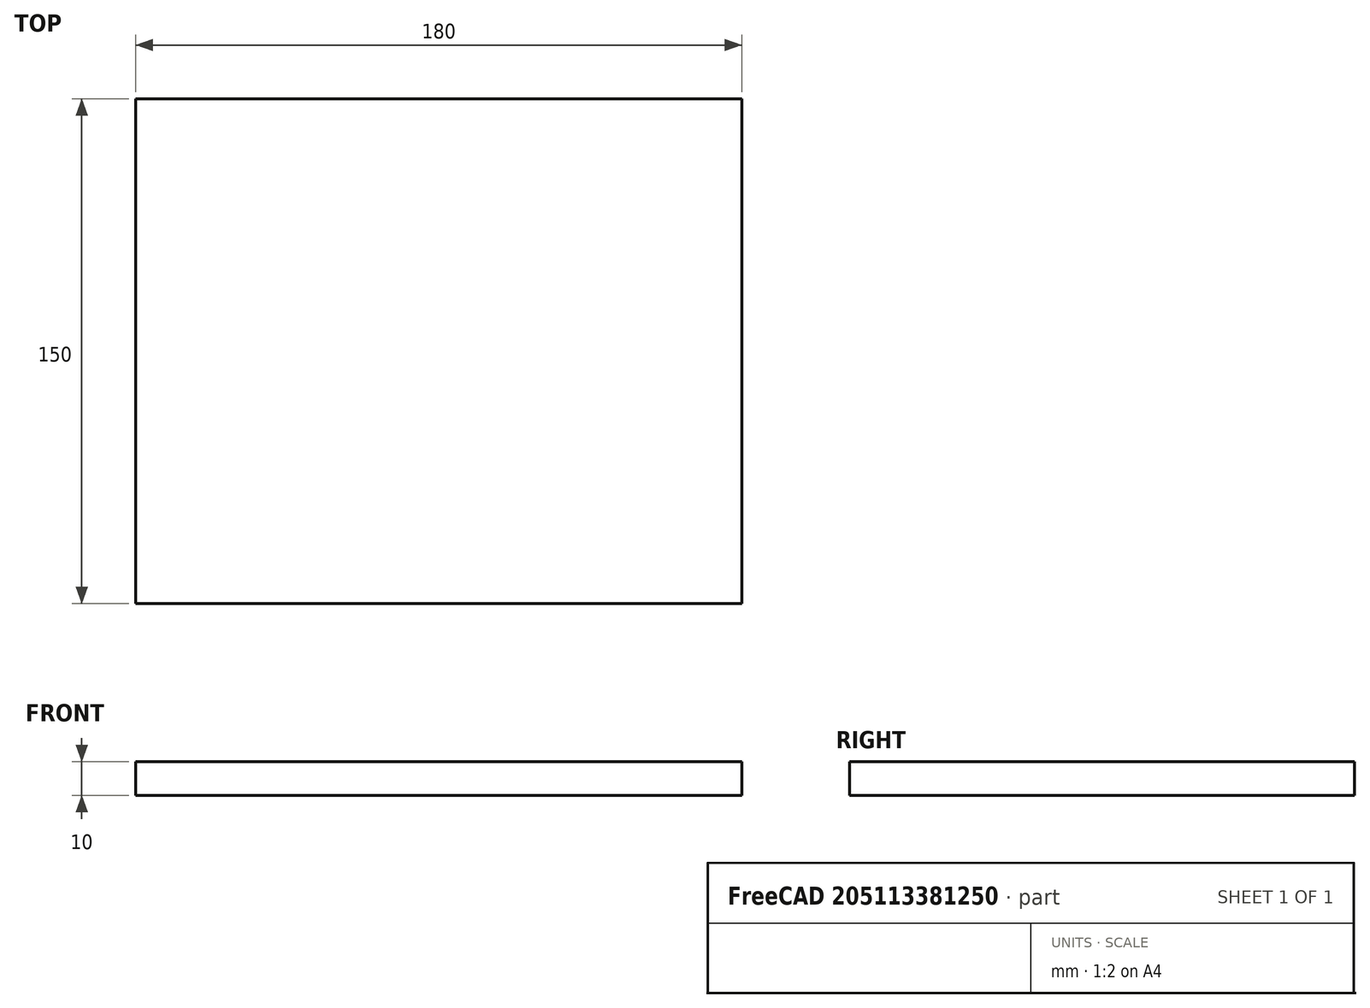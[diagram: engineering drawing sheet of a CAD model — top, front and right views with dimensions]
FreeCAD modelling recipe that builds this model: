
FCSTD DOCUMENT  (FreeCAD 0.20R29410 (Git))
Label: LightTable0
License: All rights reserved
LicenseURL: http://en.wikipedia.org/wiki/All_rights_reserved
objects: Part::Box×1, Sketcher::SketchObject×1, PartDesign::Body×1, App::Part×1
note: 3 computed .brp shape members not serialized (recipe doc carries the construction recipe); baked Part::Feature solids carry a one-line shape summary decoded from their .brp

FEATURE [Part::Box] Box  label="Cube"
  AttacherType = Attacher::AttachEngine3D
  Height = 10
  Length = 180
  Width = 150
FEATURE [Sketcher::SketchObject] Sketch
  FullyConstrained = true
  MapMode = 5
  Support = -> [XY_Plane001]
  sketch-geometry (4):
    g0: LineSegment StartX=-95 StartY=80 StartZ=0 EndX=95 EndY=80 EndZ=0
    g1: LineSegment StartX=95 StartY=80 StartZ=0 EndX=95 EndY=-80 EndZ=0
    g2: LineSegment StartX=95 StartY=-80 StartZ=0 EndX=-95 EndY=-80 EndZ=0
    g3: LineSegment StartX=-95 StartY=-80 StartZ=0 EndX=-95 EndY=80 EndZ=0
  constraints (11):
    c: Coincident(g0,g1)
    c: Coincident(g1,g2)
    c: Coincident(g2,g3)
    c: Coincident(g3,g0)
    c: Horizontal(g0)
    c: Horizontal(g2)
    c: Vertical(g1)
    c: Vertical(g3)
    c: Symmetric(g0,g1,g-1)
    c: DistanceY(g3,g3) = 160
    c: DistanceX(g2,g2) = 190
FEATURE [PartDesign::Body] Body
  Group = -> [Sketch]
  Origin = -> Origin001
FEATURE [App::Part] Part
  Group = -> [Body,Box]
  Origin = -> Origin
